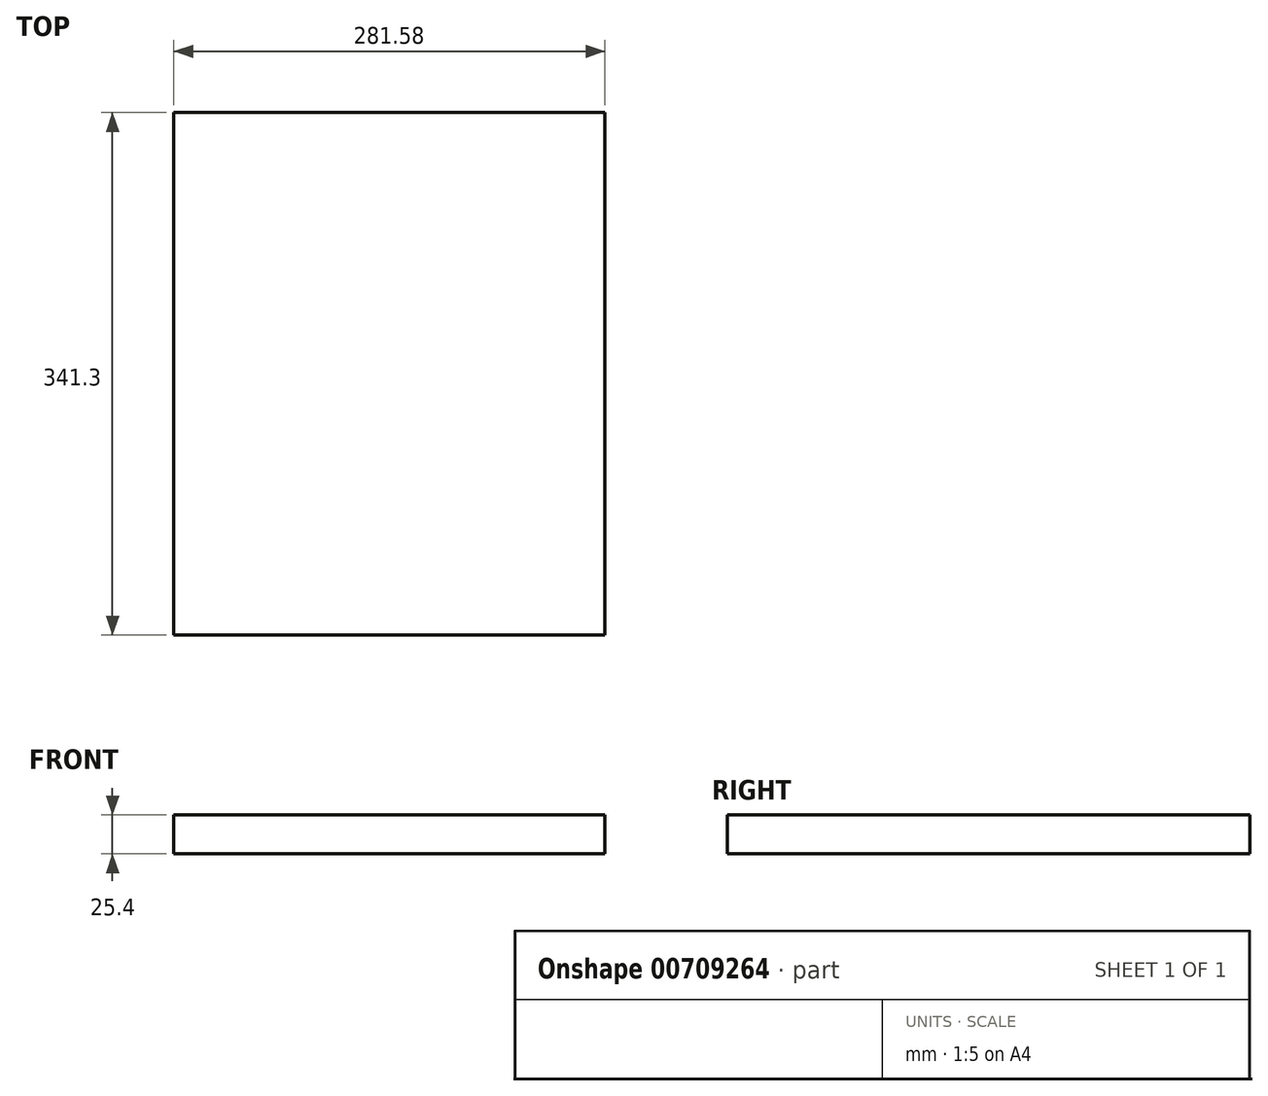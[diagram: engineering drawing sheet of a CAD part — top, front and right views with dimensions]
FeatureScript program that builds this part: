
annotation { "Feature Type Name" : "Feature", "Feature Type Description" : "" }
export const myFeature = defineFeature(function(context is Context, id is Id, definition is map)
    precondition{}
    {
        {
            var Q0;
            Q0=qCreatedBy(makeId("Top.planeOp"),FACE);
            var sketch = newSketch(context, id + "F0", { "sketchPlane" : qUnion([Q0])});
            skLineSegment(sketch, "E0.bottom", {"start": v(-140.8, 170.65) * mm, "end": v(140.8, 170.65) * mm});
            skLineSegment(sketch, "E0.top", {"start": v(-140.8, -170.65) * mm, "end": v(140.8, -170.65) * mm});
            skLineSegment(sketch, "E0.left", {"start": v(-140.8, 170.65) * mm, "end": v(-140.8, -170.65) * mm});
            skLineSegment(sketch, "E0.right", {"start": v(140.8, 170.65) * mm, "end": v(140.8, -170.65) * mm});
            skPoint(sketch, "E0.middle", {"position": v(0, 0) * mm});
            skSolve(sketch);
        }
        {
            var Q0;
            Q0 = qSketchRegion(id + "F0", true);
            extrude(context, id + "F1", {"entities" : qUnion([Q0]), "depth" : 25.4 * mm, "offsetDistance" : 25.4 * mm});
        }
    });
